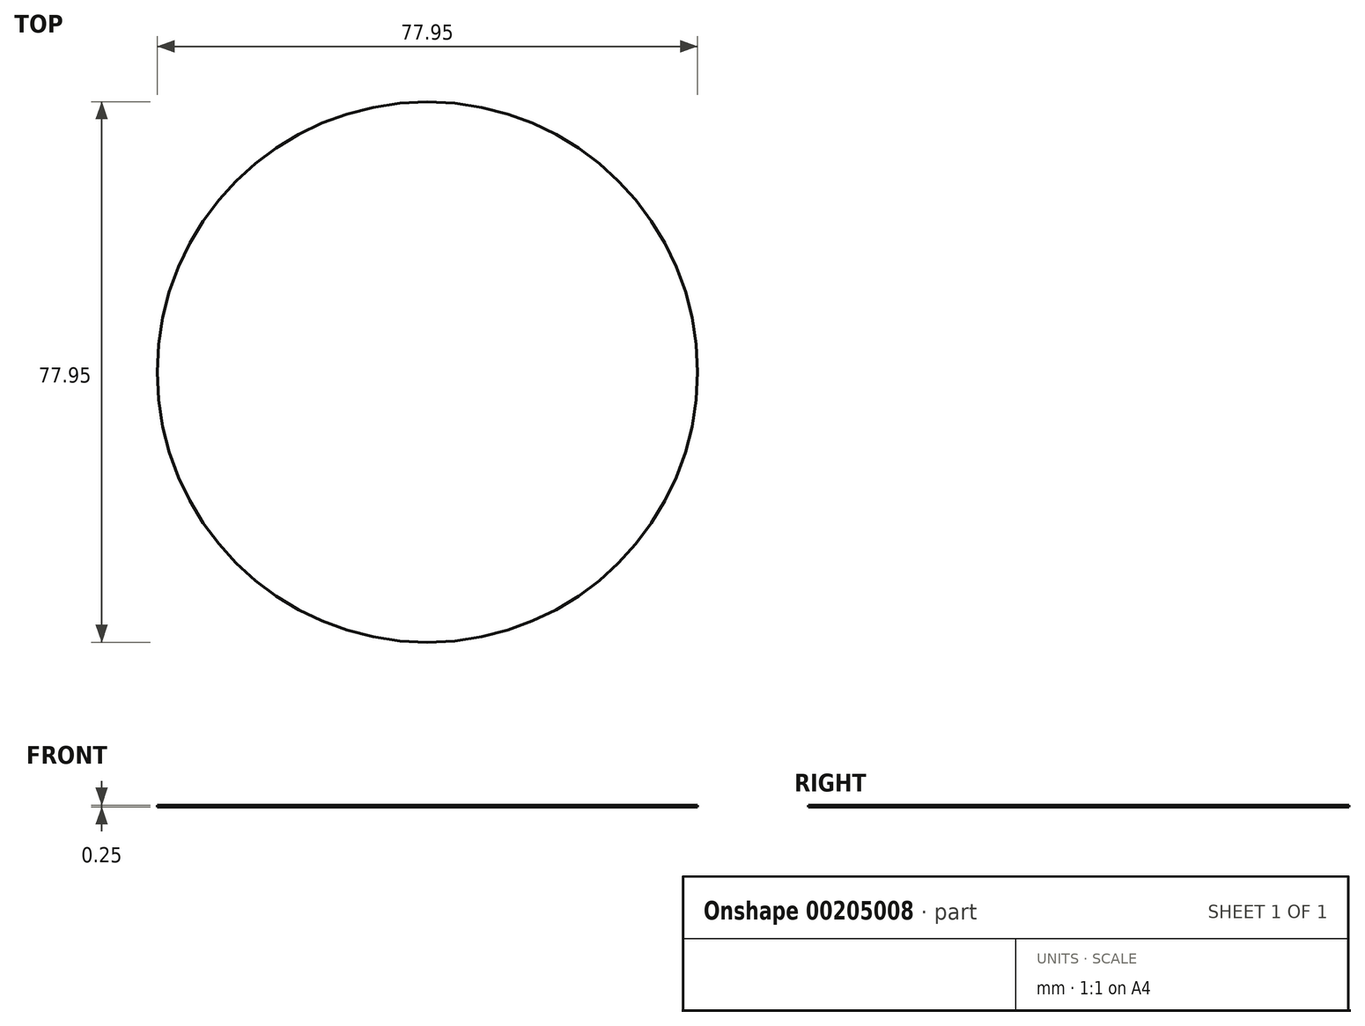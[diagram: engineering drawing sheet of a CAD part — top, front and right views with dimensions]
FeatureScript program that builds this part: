
annotation { "Feature Type Name" : "Feature", "Feature Type Description" : "" }
export const myFeature = defineFeature(function(context is Context, id is Id, definition is map)
    precondition{}
    {
        {
            var Q0;
            Q0=qCreatedBy(makeId("Top.planeOp"),FACE);
            var sketch = newSketch(context, id + "F0", { "sketchPlane" : qUnion([Q0])});
            skCircle(sketch, "E0", {"center": v(-43.5, -45.32) * mm, "radius": 38.98 * mm});
            skSolve(sketch);
        }
        {
            var Q0;
            Q0 = qSketchRegion(id + "F0", true);
            extrude(context, id + "F1", {"entities" : qUnion([Q0]), "depth" : 0.25 * mm});
        }
    });
